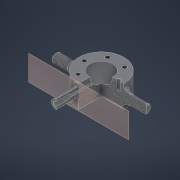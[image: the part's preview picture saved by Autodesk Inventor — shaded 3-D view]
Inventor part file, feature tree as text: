
AUTODESK INVENTOR PART (.ipt)
format: ipt  version: 2022 (Build 260153000, 153)  size: 247,296 bytes
history: native  units: mm
features: sketch x7, extrude x3, chamfer x3, other x2, revolve x2, hole x2, thread x1, mirror x1, pattern_circular x1
ambient origin geometry x8: Origin, YZ Plane, XZ Plane, XY Plane, X Axis, Y Axis, Z Axis, Center Point
bodies: Body1 (feature_tree)
feature tree (22):
  extrude  "Выдавливание8"  Depth=100.0mm
  other  "РабПлоскость16"
  revolve  "Вращение8"
  chamfer  "Фаска8"  Distance=50.0mm
  thread  "Резьба4"
  chamfer  "Фаска9"  Distance=100.0mm
  mirror  "Зеркальное отражение4"
  revolve  "Вращение9"
  other  "РабПлоскость17"
  extrude  "Выдавливание9"  Depth=10.0mm
  chamfer  "Фаска10"  Distance=35.0mm
  hole  "Отверстие6"  [1 undecoded]
  extrude  "Выдавливание10"  TaperAngle=360.0deg  [1 undecoded]
  hole  "Отверстие7"  [1 undecoded]
  pattern_circular  "Круговой массив4"  [2 undecoded]
  sketch  "Эскиз23"
  sketch  "Эскиз25"
  sketch  "Эскиз26"
  sketch  "Эскиз29"
  sketch  "Эскиз30"
  sketch  "Эскиз31"
  sketch  "Эскиз32"
note: 5 required parameter values undecoded (feature->parameter linkage not recoverable at this tier; creation-order binding heuristic only, values carry confidence <= 0.55)
